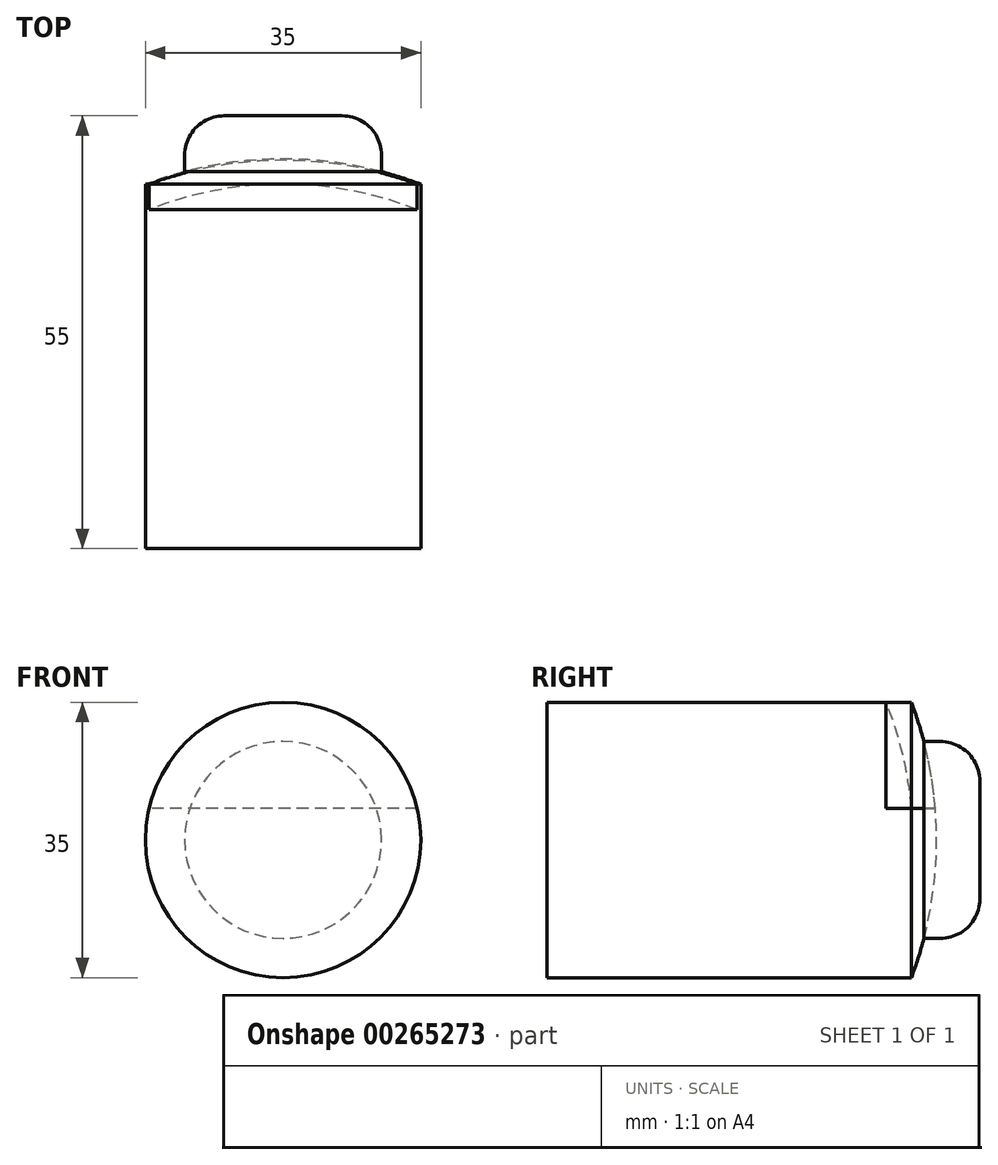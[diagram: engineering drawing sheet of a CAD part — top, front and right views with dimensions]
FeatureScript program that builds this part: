
annotation { "Feature Type Name" : "Feature", "Feature Type Description" : "" }
export const myFeature = defineFeature(function(context is Context, id is Id, definition is map)
    precondition{}
    {
        {
            var Q0;
            Q0=qCreatedBy(makeId("Front.planeOp"),FACE);
            var sketch = newSketch(context, id + "F0", { "sketchPlane" : qUnion([Q0])});
            skArc(sketch, "E0", {"start": v(0, -50) * mm, "mid": v(50, 0) * mm, "end": v(0, 50) * mm});
            skLineSegment(sketch, "E1", {"start": v(0, 0) * mm, "end": v(0, -50) * mm});
            skLineSegment(sketch, "E2", {"start": v(0, 0) * mm, "end": v(0, 50) * mm});
            skSolve(sketch);
        }
        {
            var Q0;
            Q0=makeQuery(id+"F0.imprint","IMPRINT",FACE,{"disambiguationData":[TD([[makeQuery(id+"F0.imprint","IMPRINT",EDGE,{"derivedFrom":sQuery(id+"F0.wireOp",EDGE,"E0")}),1.0]])]});
            var Q1;
            Q1=sQuery(id+"F0.wireOp",EDGE,"E2");
            revolve(context, id + "F1", {"entities" : qUnion([Q0]), "axis" : qUnion([Q1]), "revolveType" : RevolveType.FULL});
        }
        {
            var Q0;
            Q0=qCreatedBy(makeId("Front.planeOp"),FACE);
            var sketch = newSketch(context, id + "F2", { "sketchPlane" : qUnion([Q0])});
            skArc(sketch, "E3", {"start": v(-49.84, 4) * mm, "mid": v(-50, 0) * mm, "end": v(-49.84, -4) * mm});
            skLineSegment(sketch, "E4", {"start": v(-49.84, 4) * mm, "end": v(49.84, 4) * mm});
            skLineSegment(sketch, "E5", {"start": v(-49.84, -4) * mm, "end": v(49.84, -4) * mm});
            skArc(sketch, "E6.trimOffspring", {"start": v(49.84, -4) * mm, "mid": v(50, 0) * mm, "end": v(49.84, 4) * mm});
            skSolve(sketch);
        }
        {
            var Q0;
            Q0=makeQuery(id+"F2.imprint","IMPRINT",FACE,{"disambiguationData":[TD([[makeQuery(id+"F2.imprint","IMPRINT",EDGE,{"derivedFrom":sQuery(id+"F2.wireOp",EDGE,"E3")}),1.0]])]});
            extrude(context, id + "F3", {"entities" : qUnion([Q0]), "operationType" : NewBodyOperationType.REMOVE, "endBound" : BoundingType.THROUGH_ALL, "oppositeDirection" : true, "depth" : 25 * mm, "hasSecondDirection" : true, "secondDirectionBound" : SecondDirectionBoundingType.THROUGH_ALL, "secondDirectionOppositeDirection" : false, "secondDirectionDepth" : 25 * mm});
        }
        {
            var Q0;
            Q0=makeQuery(id+"F3.boolean.opBoolean","COPY",FACE,{"derivedFrom":makeQuery(id+"F3.opExtrude","SWEPT_FACE",FACE,{"disambiguationData":[OSD([sQuery(id+"F2.wireOp",EDGE,"E4")])]})});
            shell(context, id + "F4", {"entities" : qUnion([Q0]), "thickness" : 3 * mm});
        }
        {
            var Q0;
            Q0=makeQuery(id+"F3.boolean.opBoolean","COPY",FACE,{"derivedFrom":makeQuery(id+"F3.opExtrude","SWEPT_FACE",FACE,{"disambiguationData":[OSD([sQuery(id+"F2.wireOp",EDGE,"E5")])]})});
            shell(context, id + "F5", {"entities" : qUnion([Q0]), "thickness" : 3 * mm});
        }
        {
            var Q0;
            Q0=qCreatedBy(makeId("Front.planeOp"),FACE);
            var sketch = newSketch(context, id + "F6", { "sketchPlane" : qUnion([Q0])});
            skCircle(sketch, "E7", {"center": v(0, 0) * mm, "radius": 17.5 * mm});
            skSolve(sketch);
        }
        {
            var Q0;
            Q0=makeQuery(id+"F6.imprint","IMPRINT",FACE,{"disambiguationData":[TD([[makeQuery(id+"F6.imprint","IMPRINT",EDGE,{"derivedFrom":sQuery(id+"F6.wireOp",EDGE,"E7")}),1.0]])]});
            extrude(context, id + "F7", {"entities" : qUnion([Q0]), "operationType" : NewBodyOperationType.REMOVE, "endBound" : BoundingType.THROUGH_ALL, "oppositeDirection" : true, "depth" : 25 * mm});
        }
        {
            var Q0;
            Q0=qCreatedBy(makeId("Front.planeOp"),FACE);
            var sketch = newSketch(context, id + "F8", { "sketchPlane" : qUnion([Q0])});
            skCircle(sketch, "E8", {"center": v(0, 0) * mm, "radius": 49.5 * mm});
            skCircle(sketch, "E9.0", {"center": v(0, 0) * mm, "radius": 46.5 * mm});
            skLineSegment(sketch, "E10", {"start": v(0, 49.5) * mm, "end": v(0, -51.51) * mm});
            skArc(sketch, "E11", {"start": v(49.84, 4) * mm, "mid": v(0, 50) * mm, "end": v(-49.84, 4) * mm});
            skArc(sketch, "E12", {"start": v(-49.84, -4) * mm, "mid": v(0, -50) * mm, "end": v(49.84, -4) * mm});
            skLineSegment(sketch, "E13.0", {"start": v(-49.84, 4) * mm, "end": v(49.84, 4) * mm});
            skLineSegment(sketch, "E14.0", {"start": v(-49.84, -4) * mm, "end": v(49.84, -4) * mm});
            skSolve(sketch);
        }
        {
            var Q0;
            {var subQ0=sQuery(id+"F8.wireOp",EDGE,"E13.0");var subQ1=sQuery(id+"F8.wireOp",EDGE,"E8");var subQ2=makeQuery(id+"F8.imprint","INTERSECT",VERTEX,{"disambiguationData":[OD(1.0)],"derivedFrom":[subQ1,subQ0]});Q0=makeQuery(id+"F8.imprint","IMPRINT",FACE,{"disambiguationData":[TD([[makeQuery(id+"F8.imprint","IMPRINT",EDGE,{"disambiguationData":[TD([[subQ2,-1.0]])],"derivedFrom":subQ1}),1.0]])]});}
            var Q1;
            Q1=sQuery(id+"F8.wireOp",EDGE,"E10");
            revolve(context, id + "F9", {"entities" : qUnion([Q0]), "axis" : qUnion([Q1]), "revolveType" : RevolveType.FULL});
        }
        {
            var Q0;
            Q0=qCreatedBy(makeId("Front.planeOp"),FACE);
            var sketch = newSketch(context, id + "F10", { "sketchPlane" : qUnion([Q0])});
            skArc(sketch, "E15", {"start": v(0, 49.5) * mm, "mid": v(-49.5, 0) * mm, "end": v(0, -49.5) * mm});
            skArc(sketch, "E16", {"start": v(0, 48) * mm, "mid": v(-48, 0) * mm, "end": v(0, -48) * mm});
            skLineSegment(sketch, "E17", {"start": v(0, 49.5) * mm, "end": v(0, -49.5) * mm});
            skSolve(sketch);
        }
        {
            var Q0;
            {var subQ0=sQuery(id+"F10.wireOp",EDGE,"E16");Q0=makeQuery(id+"F10.imprint","IMPRINT",FACE,{"disambiguationData":[TD([[makeQuery(id+"F10.imprint","IMPRINT",EDGE,{"derivedFrom":subQ0}),1.0]])]});}
            var Q1;
            {var subQ0=sQuery(id+"F10.wireOp",EDGE,"E15");Q1=makeQuery(id+"F10.imprint","IMPRINT",FACE,{"disambiguationData":[TD([[makeQuery(id+"F10.imprint","IMPRINT",EDGE,{"derivedFrom":subQ0}),1.0]])]});}
            var Q2;
            Q2=sQuery(id+"F10.wireOp",EDGE,"E17");
            revolve(context, id + "F11", {"entities" : qUnion([Q0, Q1]), "axis" : qUnion([Q2]), "revolveType" : RevolveType.FULL});
        }
        {
            var Q0;
            Q0=qCreatedBy(makeId("Front.planeOp"),FACE);
            var sketch = newSketch(context, id + "F12", { "sketchPlane" : qUnion([Q0])});
            skCircle(sketch, "E18", {"center": v(0, 0) * mm, "radius": 17.5 * mm});
            skSolve(sketch);
        }
        {
            var Q0;
            Q0=makeQuery(id+"F12.imprint","IMPRINT",FACE,{"disambiguationData":[TD([[makeQuery(id+"F12.imprint","IMPRINT",EDGE,{"derivedFrom":sQuery(id+"F12.wireOp",EDGE,"E18")}),1.0]])]});
            extrude(context, id + "F13", {"entities" : qUnion([Q0]), "operationType" : NewBodyOperationType.INTERSECT, "endBound" : BoundingType.THROUGH_ALL, "oppositeDirection" : true, "depth" : 25 * mm});
        }
        {
            var Q0;
            Q0=qCreatedBy(makeId("Front.planeOp"),FACE);
            cPlane(context, id + "F14", {"entities" : qUnion([Q0]), "cplaneType" : CPlaneType.OFFSET, "offset" : 55 * mm, "oppositeDirection" : true, "width" : 150 * mm, "height" : 150 * mm});
        }
        {
            var Q0;
            Q0=qCreatedBy(id+"F14.planeOp",FACE);
            var sketch = newSketch(context, id + "F15", { "sketchPlane" : qUnion([Q0])});
            skCircle(sketch, "E19", {"center": v(0, 0) * mm, "radius": 12.5 * mm});
            skSolve(sketch);
        }
        {
            var Q0;
            Q0=makeQuery(id+"F15.imprint","IMPRINT",FACE,{"disambiguationData":[TD([[makeQuery(id+"F15.imprint","IMPRINT",EDGE,{"derivedFrom":sQuery(id+"F15.wireOp",EDGE,"E19")}),1.0]])]});
            extrude(context, id + "F16", {"entities" : qUnion([Q0]), "endBound" : BoundingType.UP_TO_NEXT, "depth" : 25 * mm});
        }
        {
            var Q0;
            Q0=makeQuery(id+"F16.opExtrude","CAP_EDGE",EDGE,{"disambiguationData":[OSD([sQuery(id+"F15.wireOp",EDGE,"E19")])],"isStart":true});
            fillet(context, id + "F17", {"entities" : qUnion([Q0]), "radius" : 5 * mm, "tangentPropagation" : true, "allowEdgeOverflow" : false});
        }
    });
